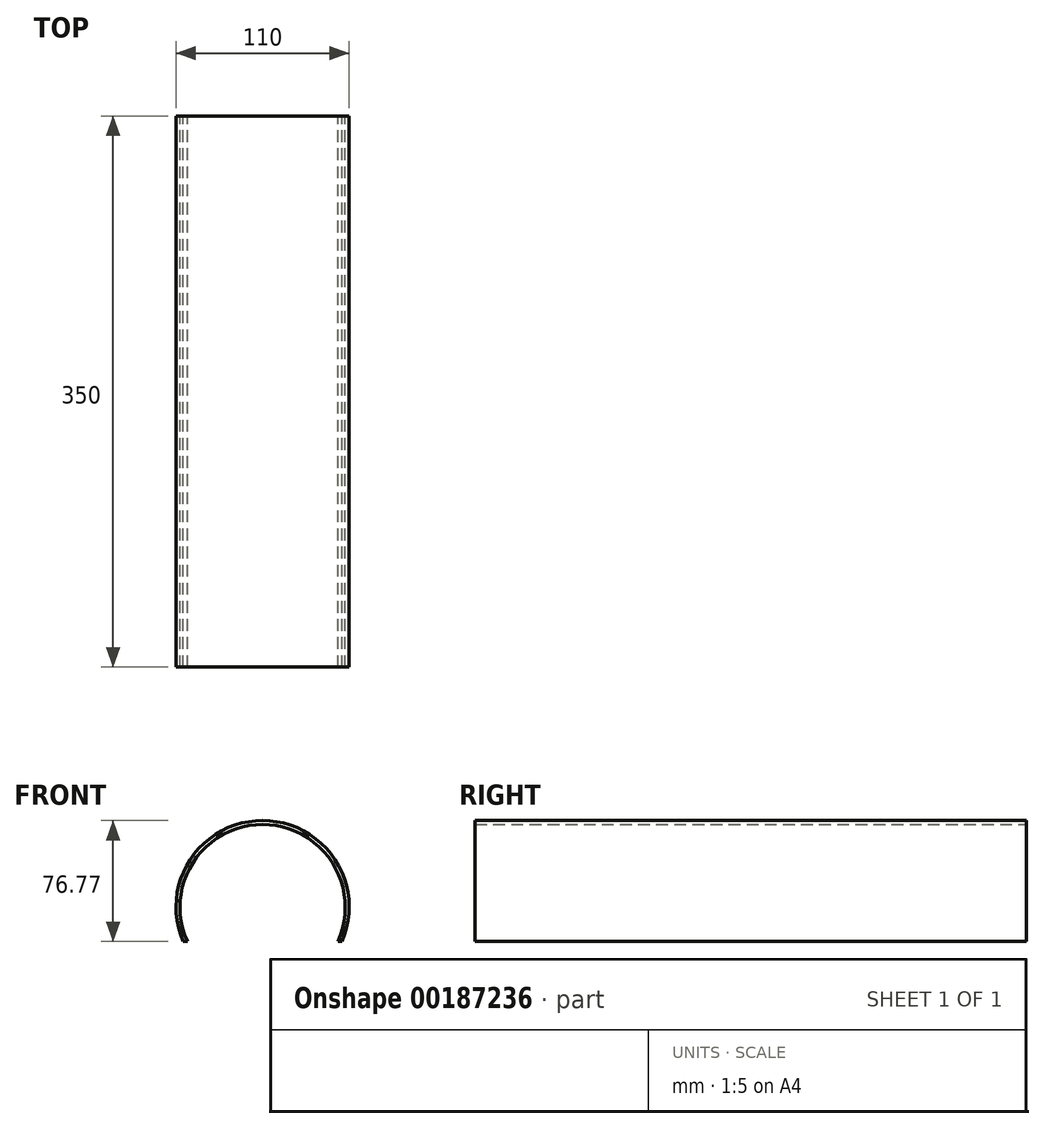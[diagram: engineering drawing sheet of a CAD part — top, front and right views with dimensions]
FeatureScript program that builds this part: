
annotation { "Feature Type Name" : "Feature", "Feature Type Description" : "" }
export const myFeature = defineFeature(function(context is Context, id is Id, definition is map)
    precondition{}
    {
        {
            var Q0;
            Q0=qCreatedBy(makeId("Front.planeOp"),FACE);
            var sketch = newSketch(context, id + "F0", { "sketchPlane" : qUnion([Q0])});
            skArc(sketch, "E0", {"start": v(50.5, -21.77) * mm, "mid": v(0, 55) * mm, "end": v(-50.5, -21.77) * mm});
            skArc(sketch, "E1", {"start": v(47.77, -21.77) * mm, "mid": v(0, 52.5) * mm, "end": v(-47.77, -21.77) * mm});
            skLineSegment(sketch, "E2", {"start": v(-47.77, -21.77) * mm, "end": v(-50.5, -21.77) * mm});
            skLineSegment(sketch, "E3", {"start": v(47.77, -21.77) * mm, "end": v(50.5, -21.77) * mm});
            skPoint(sketch, "E4.center.orphan", {"position": v(0, -55) * mm});
            skSolve(sketch);
        }
        {
            var Q0;
            Q0=makeQuery(id+"F0.imprint","IMPRINT",FACE,{"disambiguationData":[TD([[makeQuery(id+"F0.imprint","IMPRINT",EDGE,{"derivedFrom":sQuery(id+"F0.wireOp",EDGE,"E0")}),1.0]])]});
            extrude(context, id + "F1", {"entities" : qUnion([Q0]), "depth" : 350 * mm});
        }
    });
